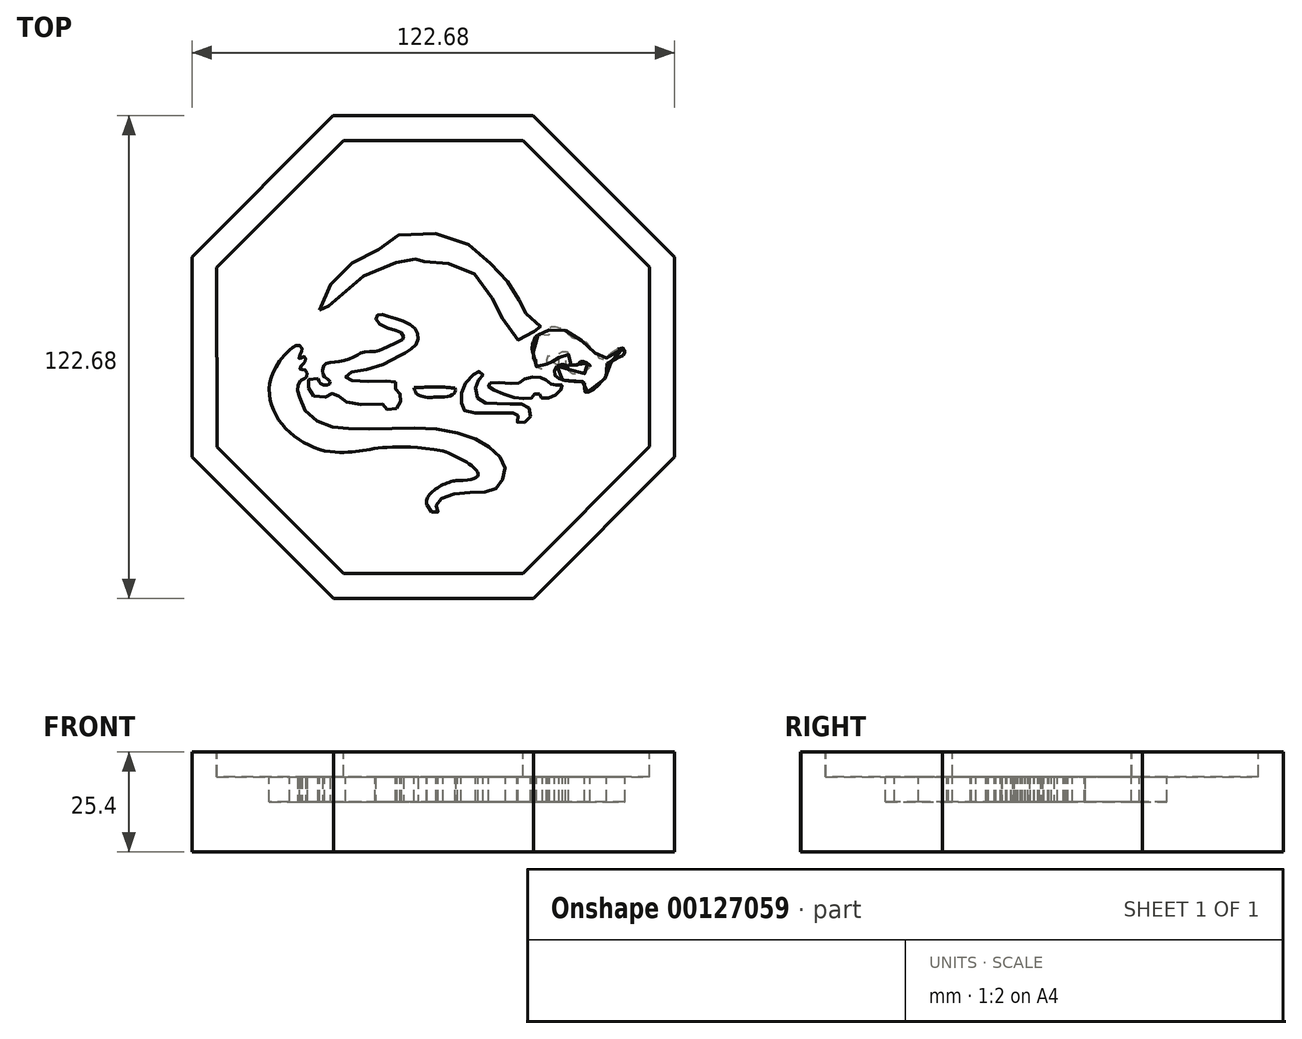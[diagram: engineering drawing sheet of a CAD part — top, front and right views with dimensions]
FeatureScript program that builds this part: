
annotation { "Feature Type Name" : "Feature", "Feature Type Description" : "" }
export const myFeature = defineFeature(function(context is Context, id is Id, definition is map)
    precondition{}
    {
        {
            var Q0;
            Q0=qCreatedBy(makeId("Top.planeOp"),FACE);
            var sketch = newSketch(context, id + "F0", { "sketchPlane" : qUnion([Q0])});
            skCircle(sketch, "E0.cCircle", {"center": v(0, 0) * mm, "radius": 61.32 * mm, "construction": true});
            skLineSegment(sketch, "E0.0", {"start": v(-61.3, -25.44) * mm, "end": v(-61.34, 25.36) * mm});
            skLineSegment(sketch, "E0.1", {"start": v(-61.34, 25.36) * mm, "end": v(-25.44, 61.3) * mm});
            skLineSegment(sketch, "E0.2", {"start": v(-25.44, 61.3) * mm, "end": v(25.36, 61.34) * mm});
            skLineSegment(sketch, "E0.3", {"start": v(25.36, 61.34) * mm, "end": v(61.3, 25.44) * mm});
            skLineSegment(sketch, "E0.4", {"start": v(61.3, 25.44) * mm, "end": v(61.34, -25.36) * mm});
            skLineSegment(sketch, "E0.5", {"start": v(61.34, -25.36) * mm, "end": v(25.44, -61.3) * mm});
            skLineSegment(sketch, "E0.6", {"start": v(25.44, -61.3) * mm, "end": v(-25.36, -61.34) * mm});
            skLineSegment(sketch, "E0.7", {"start": v(-25.36, -61.34) * mm, "end": v(-61.3, -25.44) * mm});
            skPoint(sketch, "E0.0.midPoint", {"position": v(-61.32, -0.04) * mm});
            skSolve(sketch);
        }
        {
            var Q0;
            Q0=qSketchRegion(id+"F0",true);
            extrude(context, id + "F1", {"entities" : qUnion([Q0]), "depth" : 25.4 * mm});
        }
        {
            var Q0;
            Q0=makeQuery(id+"F1.opExtrude","CAP_FACE",FACE,{"disambiguationData":[OSD([sQuery(id+"F0.wireOp",EDGE,"E0.0"),sQuery(id+"F0.wireOp",EDGE,"E0.1"),sQuery(id+"F0.wireOp",EDGE,"E0.2"),sQuery(id+"F0.wireOp",EDGE,"E0.3"),sQuery(id+"F0.wireOp",EDGE,"E0.4"),sQuery(id+"F0.wireOp",EDGE,"E0.5"),sQuery(id+"F0.wireOp",EDGE,"E0.6"),sQuery(id+"F0.wireOp",EDGE,"E0.7")])],"isStart":false});
            var sketch = newSketch(context, id + "F2", { "sketchPlane" : qUnion([Q0])});
            skLineSegment(sketch, "E1.0", {"start": v(-54.96, -22.8) * mm, "end": v(-54.99, 22.73) * mm});
            skLineSegment(sketch, "E1.1", {"start": v(-22.73, -54.99) * mm, "end": v(-54.96, -22.8) * mm});
            skLineSegment(sketch, "E1.2", {"start": v(-54.99, 22.73) * mm, "end": v(-22.8, 54.96) * mm});
            skLineSegment(sketch, "E1.3", {"start": v(22.8, -54.96) * mm, "end": v(-22.73, -54.99) * mm});
            skLineSegment(sketch, "E1.4", {"start": v(-22.8, 54.96) * mm, "end": v(22.73, 54.99) * mm});
            skLineSegment(sketch, "E1.5", {"start": v(22.73, 54.99) * mm, "end": v(54.96, 22.8) * mm});
            skLineSegment(sketch, "E1.6", {"start": v(54.96, 22.8) * mm, "end": v(54.99, -22.73) * mm});
            skLineSegment(sketch, "E1.7", {"start": v(54.99, -22.73) * mm, "end": v(22.8, -54.96) * mm});
            skSolve(sketch);
        }
        {
            var Q0;
            Q0=qSketchRegion(id+"F2",true);
            extrude(context, id + "F3", {"entities" : qUnion([Q0]), "operationType" : NewBodyOperationType.REMOVE, "oppositeDirection" : true, "depth" : 6.35 * mm});
        }
        {
            var Q0;
            Q0=makeQuery(id+"F3.boolean.opBoolean","COPY",FACE,{"derivedFrom":makeQuery(id+"F3.opExtrude","CAP_FACE",FACE,{"disambiguationData":[OSD([sQuery(id+"F2.wireOp",EDGE,"E1.0"),sQuery(id+"F2.wireOp",EDGE,"E1.1"),sQuery(id+"F2.wireOp",EDGE,"E1.2"),sQuery(id+"F2.wireOp",EDGE,"E1.3"),sQuery(id+"F2.wireOp",EDGE,"E1.4"),sQuery(id+"F2.wireOp",EDGE,"E1.5"),sQuery(id+"F2.wireOp",EDGE,"E1.6"),sQuery(id+"F2.wireOp",EDGE,"E1.7")])],"isStart":false})});
            var sketch = newSketch(context, id + "F4", { "sketchPlane" : qUnion([Q0])});
            skFitSpline(sketch, "E2", {"points": [v(-28.85, 11.93) * mm, v(-28.65, 10.93) * mm, v(-27.75, 10.83) * mm, v(-26.96, 12.32) * mm, v(-19.19, 19.6) * mm, v(-14.2, 22.18) * mm, v(-7.74, 24.67) * mm, v(-5.74, 25.27) * mm, v(-4.55, 25.07) * mm, v(-4.35, 23.88) * mm, v(-3.55, 22.68) * mm, v(-2.66, 23.88) * mm, v(-0.18, 24.67) * mm, v(3.02, 24.08) * mm, v(6.9, 22.58) * mm, v(10.3, 21.19) * mm, v(12.48, 18.4) * mm, v(15.57, 14.22) * mm, v(17.16, 11.93) * mm, v(17.66, 9.34) * mm, v(21.05, 3.86) * mm, v(21.54, 4.36) * mm, v(21.54, 5.25) * mm, v(22.94, 6.35) * mm, v(26.32, 6.35) * mm, v(27.02, 6.05) * mm, v(27.72, 6.35) * mm, v(27.42, 7.54) * mm, v(25.83, 9.34) * mm, v(24.43, 10.93) * mm, v(23.34, 10.93) * mm, v(22.64, 10.93) * mm, v(22.34, 12.62) * mm, v(21.54, 14.91) * mm, v(20.15, 16.4) * mm, v(18.95, 19) * mm, v(17.46, 21.39) * mm, v(14.77, 23.58) * mm, v(11.49, 26.27) * mm, v(8.1, 29.16) * mm, v(2.22, 31.05) * mm, v(-4.65, 31.64) * mm, v(-10.82, 30.05) * mm, v(-12.81, 28.06) * mm, v(-14.7, 27.06) * mm, v(-18.99, 25.07) * mm, v(-22.77, 22.18) * mm, v(-25.96, 18.8) * mm, v(-28.15, 13.72) * mm, v(-28.85, 11.93) * mm]});
            skFitSpline(sketch, "E3", {"points": [v(-36.52, 1.76) * mm, v(-27.55, -23.83) * mm], "startDerivative": vector(-34.66, -31.97) * mm, "endDerivative": vector(31.67, -7.17) * mm});
            skFitSpline(sketch, "E4", {"points": [v(-27.55, -23.83) * mm, v(2.52, -23.83) * mm], "startDerivative": vector(32.57, -5.08) * mm, "endDerivative": vector(56.77, -8.66) * mm});
            skFitSpline(sketch, "E5", {"points": [v(2.52, -23.83) * mm, v(6.2, -31.4) * mm], "startDerivative": vector(14.64, -5.68) * mm, "endDerivative": vector(-34.06, -0.6) * mm});
            skFitSpline(sketch, "E6", {"points": [v(6.2, -31.4) * mm, v(-1.56, -37.57) * mm], "startDerivative": vector(-8.37, 0) * mm, "endDerivative": vector(3.59, -8.66) * mm});
            skFitSpline(sketch, "E7", {"points": [v(-1.56, -37.57) * mm, v(-0.88, -38.8) * mm, v(0.47, -39.77) * mm, v(1.16, -39.46) * mm, v(1.03, -38.61) * mm, v(0.72, -37.57) * mm, v(1.9, -36.1) * mm, v(5.64, -34.75) * mm, v(11.35, -34.4) * mm, v(15.04, -33.94) * mm, v(16.89, -32.44) * mm, v(18.23, -29.4) * mm, v(17.75, -26.53) * mm, v(14.74, -23.27) * mm, v(9.76, -20.46) * mm, v(0.68, -18.22) * mm, v(-10.2, -18.16) * mm, v(-20.9, -18.19) * mm, v(-26.82, -17.44) * mm, v(-31.99, -14.34) * mm, v(-34.02, -10.17) * mm], "startDerivative": vector(17.57, -40.75) * mm, "endDerivative": vector(-21.1, 81.39) * mm});
            skFitSpline(sketch, "E8", {"points": [v(-36.52, 1.76) * mm, v(-35.2, 2.72) * mm, v(-33.86, 2.96) * mm, v(-33.33, 1.76) * mm, v(-33.68, 1.04) * mm, v(-34.1, -0.46) * mm, v(-33.17, 0) * mm, v(-32.53, 0) * mm, v(-32.53, -0.92) * mm, v(-32.8, -1.4) * mm, v(-33.59, -2.2) * mm, v(-33.86, -3.06) * mm, v(-33.23, -3.22) * mm, v(-32.33, -3.46) * mm, v(-32.18, -5.02) * mm, v(-32.6, -5.35) * mm, v(-34.2, -6.66) * mm, v(-34.02, -10.17) * mm], "startDerivative": vector(14.83, 18.2) * mm, "endDerivative": vector(12.64, -39.5) * mm});
            skFitSpline(sketch, "E9", {"points": [v(-29.28, -5.5) * mm, v(-28.85, -6.44) * mm, v(-27.95, -7.14) * mm, v(-26.55, -6.97) * mm, v(-26.25, -6.24) * mm, v(-27.35, -5.28) * mm, v(-28.05, -4.15) * mm, v(-27.75, -2.05) * mm, v(-25.69, -1.35) * mm, v(-22.96, -0.92) * mm, v(-19.8, 0.2) * mm, v(-18.08, 1.1) * mm, v(-14.79, 1.44) * mm], "startDerivative": vector(5.68, -15.31) * mm, "endDerivative": vector(32.55, 0.81) * mm});
            skFitSpline(sketch, "E10", {"points": [v(-29.28, -5.5) * mm, v(-31.17, -5.24) * mm, v(-31.94, -6.64) * mm, v(-31.84, -7.57) * mm, v(-31.04, -9.1) * mm, v(-30.08, -10.03) * mm, v(-27.42, -10.2) * mm, v(-26.32, -9.93) * mm, v(-25.56, -9.2) * mm, v(-24.7, -9.36) * mm, v(-23.76, -10.16) * mm, v(-22.27, -11.26) * mm, v(-21.04, -12.02) * mm, v(-13.16, -11.92) * mm, v(-12.26, -12.49) * mm, v(-11.86, -13.25) * mm, v(-9.8, -13.52) * mm, v(-9.24, -12.75) * mm, v(-8.64, -11.72) * mm, v(-8.1, -10.9) * mm, v(-8.24, -9.66) * mm, v(-9.14, -8.9) * mm, v(-9.6, -8.53) * mm, v(-9.24, -7.1) * mm, v(-9.44, -6.44) * mm, v(-10.04, -6.34) * mm, v(-12.2, -6.14) * mm, v(-17.88, -6.24) * mm, v(-21.23, -5.83) * mm, v(-22.13, -5.5) * mm, v(-22.17, -4.78) * mm, v(-21.53, -4.05) * mm, v(-18.73, -3.5) * mm, v(-14.02, -2.41) * mm, v(-8.4, 0.37) * mm], "startDerivative": vector(-68.08, 25.5) * mm, "endDerivative": vector(91.95, 61.99) * mm});
            skFitSpline(sketch, "E11", {"points": [v(-14.79, 1.44) * mm, v(-13.58, 1.7) * mm, v(-8.42, 4.13) * mm, v(-7.54, 4.84) * mm, v(-7.92, 5.9) * mm, v(-9.31, 6.65) * mm, v(-13.87, 8.57) * mm, v(-14.55, 10.17) * mm, v(-13.49, 10.85) * mm, v(-11.15, 10.26) * mm, v(-7.48, 9.01) * mm, v(-4.7, 7.27) * mm, v(-3.92, 5.43) * mm, v(-4.07, 3.63) * mm, v(-6.53, 1.44) * mm, v(-8.4, 0.37) * mm], "startDerivative": vector(18.95, 1.49) * mm, "endDerivative": vector(-26.97, -14.12) * mm});
            skFitSpline(sketch, "E12", {"points": [v(-4.9, -7.8) * mm, v(5.56, -7.93) * mm], "startDerivative": vector(10.63, 0.56) * mm, "endDerivative": vector(10.02, -1.45) * mm});
            skFitSpline(sketch, "E13", {"points": [v(5.56, -7.93) * mm, v(5.4, -9.14) * mm, v(3.34, -10.08) * mm, v(0.6, -10.19) * mm, v(-1.41, -10.28) * mm, v(-3.13, -9.89) * mm, v(-4.3, -9.24) * mm, v(-4.9, -7.8) * mm], "startDerivative": vector(1, -11.02) * mm, "endDerivative": vector(-3.29, 12.26) * mm});
            skFitSpline(sketch, "E14", {"points": [v(10.2, -4.49) * mm, v(11.12, -3.78) * mm, v(12.17, -3.7) * mm, v(12.58, -4.6) * mm, v(11.98, -5.38) * mm, v(10.94, -6.91) * mm, v(10.86, -9.45) * mm, v(12.43, -11.46) * mm, v(15.45, -11.76) * mm, v(20.04, -11.95) * mm, v(23.17, -12.17) * mm, v(24.52, -13.44) * mm, v(24.55, -15.53) * mm, v(22.87, -16.69) * mm, v(21.42, -16.69) * mm, v(21.38, -15.6) * mm, v(21.38, -14.6) * mm, v(20.52, -14.3) * mm, v(18.02, -14.19) * mm, v(12.95, -14.26) * mm, v(8.33, -13.85) * mm, v(7.32, -12.7) * mm, v(7.06, -10.08) * mm, v(7.77, -7.29) * mm, v(10.2, -4.49) * mm]});
            skFitSpline(sketch, "E15", {"points": [v(21.8, -6.58) * mm, v(18.96, -6.65) * mm, v(14.6, -6.61) * mm, v(14.1, -6.95) * mm, v(14.15, -7.62) * mm, v(15.64, -8.4) * mm, v(19.78, -10.12) * mm, v(23.14, -10.57) * mm, v(25.26, -10.23) * mm, v(25.75, -9.41) * mm, v(26.83, -9.19) * mm, v(27.05, -10.08) * mm, v(28.02, -10.53) * mm, v(29.96, -10.27) * mm, v(31.86, -8.96) * mm, v(32.87, -7.55) * mm, v(32.46, -7.02) * mm, v(31, -7.1) * mm, v(30.07, -7.02) * mm, v(28.8, -5.98) * mm, v(27.76, -5.35) * mm, v(25.63, -5) * mm, v(23.17, -5.53) * mm, v(21.8, -6.58) * mm]});
            skFitSpline(sketch, "E16", {"points": [v(31.4, -2.34) * mm, v(30.8, -3.35) * mm, v(30.96, -4.76) * mm, v(32.13, -5.58) * mm, v(34, -6.08) * mm, v(34.48, -6.1) * mm, v(36.3, -6.2) * mm, v(38.21, -6.3) * mm, v(38.43, -6.99) * mm, v(38.46, -8.24) * mm, v(38.56, -8.93) * mm, v(39.12, -8.96) * mm, v(40.63, -8.34) * mm, v(42.16, -6.86) * mm, v(43.64, -5.39) * mm, v(44.01, -4.32) * mm, v(44.17, -1.6) * mm, v(45.14, -1.12) * mm, v(47.43, 0.13) * mm, v(48.66, 0.76) * mm, v(48.31, 2.1) * mm, v(47.59, 2.36) * mm, v(45.86, 1.45) * mm, v(44.33, 0.1) * mm, v(43.64, -0.56) * mm, v(42.95, -0.65) * mm, v(42.13, -0.2) * mm, v(41.57, 0.7) * mm, v(40.85, 1.26) * mm, v(39.97, 2.36) * mm, v(39.15, 3.43) * mm, v(37.65, 4.15) * mm, v(36.01, 4.65) * mm, v(34.98, 5.12) * mm, v(33.91, 6.44) * mm, v(31.72, 7.47) * mm, v(30.3, 7.7) * mm, v(29.43, 7.29) * mm, v(29.46, 6.31) * mm, v(29.43, 5.56) * mm, v(28.42, 5.47) * mm, v(27.2, 5.69) * mm, v(26.23, 5.37) * mm, v(25.54, 4.18) * mm, v(25.1, 1.92) * mm, v(25.44, 0.6) * mm, v(25.6, -0.65) * mm, v(26.13, -0.96) * mm, v(26.13, -1.65) * mm, v(26.2, -2.44) * mm, v(26.8, -2.88) * mm, v(28.17, -2.88) * mm, v(28.33, -2.1) * mm, v(28.77, -1.97) * mm, v(28.83, -0.8) * mm, v(29.27, 0.48) * mm, v(29.5, -0.2) * mm, v(30.05, -0.96) * mm, v(30.78, -1.5) * mm, v(31.65, -1.97) * mm, v(31.97, -1.72) * mm, v(31.9, -1.1) * mm, v(31.97, 0.2) * mm, v(31.94, 0.98) * mm, v(33.29, 1.42) * mm, v(34.1, 1.2) * mm, v(34.35, 0.54) * mm, v(33.85, -0.2) * mm, v(33.57, -1.22) * mm, v(33.88, -1.97) * mm, v(35.42, -2) * mm, v(36.96, -1.84) * mm, v(37.2, -1.25) * mm, v(38.56, -1.3) * mm, v(39.62, -1.97) * mm, v(39.87, -2.31) * mm, v(39.37, -3) * mm, v(38.87, -3.6) * mm, v(38.52, -4.2) * mm, v(37.18, -4.26) * mm, v(35.54, -4.35) * mm, v(34.89, -3.88) * mm, v(34.29, -2.9) * mm, v(33.88, -2.19) * mm, v(32.85, -1.94) * mm, v(31.84, -2.16) * mm, v(31.4, -2.34) * mm]});
            skSolve(sketch);
        }
        {
            var Q0;
            Q0 = qSketchRegion(id + "F4", true);
            extrude(context, id + "F5", {"entities" : qUnion([Q0]), "operationType" : NewBodyOperationType.REMOVE, "oppositeDirection" : true, "depth" : 6.35 * mm});
        }
    });
